# Revit family: Legrand XL³-S 160 surface mounting
name_source: partatom
category: Equipement électrique
units: mm (PartAtom-declared; Revit-internal decimal feet)

## family parameters
Basée sur le plan de construction = Non
Configuration du panneau = Deux colonnes, circuits au sein
Cote de connecteur circulaire = Utiliser le diamètre
Couper avec des vides une fois chargée = Non
Numéro OmniClass = 23.80.30.11.17
Partagée = Non
Point de calcul de pièce = Non
Titre OmniClass = Distribution Boards and Control Panels
Toujours verticalement = Oui
Type d'élément = Tableau de raccordement

## types (12) — shared parameters
ETIM Class 6.0 = EC000261
Fabricant = Legrand
General Conditions of Use = https://export.legrand.com
IK = 07
IP = 40
Image du type = XL3S160_saillie_337204_p_230125.jpg
Material = Steel
RAL = 9003
URL = www.legrand.fr
depth = 135 mm  [stored 0.442913 ft]
distance side installation zone = 135 mm  [stored 0.442913 ft]
door = Oui
zero-valued in all types: Elévation par défaut

## per-type parameters (varying)
- Distribution envelope - XL³ S 160 Métal - surface mounting - 24 modules - 2 rows: Cabinet 337202=Oui; Cabinet 337203=Non; Cabinet 337204=Non; Cabinet 337205=Non; Cabinet 337206=Non; Cabinet 337207=Non; Cabinet 337208=Non; Cabinet 337214=Non; Cabinet 337215=Non; Cabinet 337216=Non; Cabinet 337217=Non; Cabinet 337218=Non; Description=337202  Distribution envelope - XL³ S 160 Métal - surface mounting - 24 modules - 2 rows; depth installation zone=730 mm  [stored 2.39501 ft]; distance before installation zone=595 mm  [stored 1.9521 ft]; door 337252=Oui; door 337253=Non; door 337254=Non; door 337255=Non; door 337256=Non; door 337257=Non; door 337258=Non; door 337264=Non; door 337265=Non; door 337266=Non; door 337267=Non; door 337268=Non; height=440 mm  [stored 1.44357 ft]; width=595 mm  [stored 1.9521 ft]; width installation zone=865 mm  [stored 2.83793 ft]
- Distribution envelope - XL³ S 160 Métal - surface mounting - 24 modules - 3 rows: Cabinet 337202=Non; Cabinet 337203=Oui; Cabinet 337204=Non; Cabinet 337205=Non; Cabinet 337206=Non; Cabinet 337207=Non; Cabinet 337208=Non; Cabinet 337214=Non; Cabinet 337215=Non; Cabinet 337216=Non; Cabinet 337217=Non; Cabinet 337218=Non; Description=337203  Distribution envelope - XL³ S 160 Métal - surface mounting - 24 modules - 3 rows; depth installation zone=730 mm  [stored 2.39501 ft]; distance before installation zone=595 mm  [stored 1.9521 ft]; door 337252=Non; door 337253=Oui; door 337254=Non; door 337255=Non; door 337256=Non; door 337257=Non; door 337258=Non; door 337264=Non; door 337265=Non; door 337266=Non; door 337267=Non; door 337268=Non; height=590 mm  [stored 1.9357 ft]; width=595 mm  [stored 1.9521 ft]; width installation zone=865 mm  [stored 2.83793 ft]
- Distribution envelope - XL³ S 160 Métal - surface mounting - 24 modules - 4 rows: Cabinet 337202=Non; Cabinet 337203=Non; Cabinet 337204=Oui; Cabinet 337205=Non; Cabinet 337206=Non; Cabinet 337207=Non; Cabinet 337208=Non; Cabinet 337214=Non; Cabinet 337215=Non; Cabinet 337216=Non; Cabinet 337217=Non; Cabinet 337218=Non; Description=337204  Distribution envelope - XL³ S 160 Métal - surface mounting - 24 modules - 4 rows; depth installation zone=730 mm  [stored 2.39501 ft]; distance before installation zone=595 mm  [stored 1.9521 ft]; door 337252=Non; door 337253=Non; door 337254=Oui; door 337255=Non; door 337256=Non; door 337257=Non; door 337258=Non; door 337264=Non; door 337265=Non; door 337266=Non; door 337267=Non; door 337268=Non; height=740 mm  [stored 2.42782 ft]; width=595 mm  [stored 1.9521 ft]; width installation zone=865 mm  [stored 2.83793 ft]
- Distribution envelope - XL³ S 160 Métal - surface mounting - 24 modules - 5 rows: Cabinet 337202=Non; Cabinet 337203=Non; Cabinet 337204=Non; Cabinet 337205=Oui; Cabinet 337206=Non; Cabinet 337207=Non; Cabinet 337208=Non; Cabinet 337214=Non; Cabinet 337215=Non; Cabinet 337216=Non; Cabinet 337217=Non; Cabinet 337218=Non; Description=337205  Distribution envelope - XL³ S 160 Métal - surface mounting - 24 modules - 6 rows; depth installation zone=730 mm  [stored 2.39501 ft]; distance before installation zone=595 mm  [stored 1.9521 ft]; door 337252=Non; door 337253=Non; door 337254=Non; door 337255=Oui; door 337256=Non; door 337257=Non; door 337258=Non; door 337264=Non; door 337265=Non; door 337266=Non; door 337267=Non; door 337268=Non; height=890 mm  [stored 2.91995 ft]; width=595 mm  [stored 1.9521 ft]; width installation zone=865 mm  [stored 2.83793 ft]
- Distribution envelope - XL³ S 160 Métal - surface mounting - 24 modules - 6 rows: Cabinet 337202=Non; Cabinet 337203=Non; Cabinet 337204=Non; Cabinet 337205=Non; Cabinet 337206=Oui; Cabinet 337207=Non; Cabinet 337208=Non; Cabinet 337214=Non; Cabinet 337215=Non; Cabinet 337216=Non; Cabinet 337217=Non; Cabinet 337218=Non; Description=337206  Distribution envelope - XL³ S 160 Métal - surface mounting - 24 modules - 7 rows; depth installation zone=730 mm  [stored 2.39501 ft]; distance before installation zone=595 mm  [stored 1.9521 ft]; door 337252=Non; door 337253=Non; door 337254=Non; door 337255=Non; door 337256=Oui; door 337257=Non; door 337258=Non; door 337264=Non; door 337265=Non; door 337266=Non; door 337267=Non; door 337268=Non; height=1040 mm  [stored 3.41207 ft]; width=595 mm  [stored 1.9521 ft]; width installation zone=865 mm  [stored 2.83793 ft]
- Distribution envelope - XL³ S 160 Métal - surface mounting - 24 modules - 7 rows: Cabinet 337202=Non; Cabinet 337203=Non; Cabinet 337204=Non; Cabinet 337205=Non; Cabinet 337206=Non; Cabinet 337207=Oui; Cabinet 337208=Non; Cabinet 337214=Non; Cabinet 337215=Non; Cabinet 337216=Non; Cabinet 337217=Non; Cabinet 337218=Non; Description=337207  Distribution envelope - XL³ S 160 Métal - surface mounting - 24 modules - 7 rows; depth installation zone=730 mm  [stored 2.39501 ft]; distance before installation zone=595 mm  [stored 1.9521 ft]; door 337252=Non; door 337253=Non; door 337254=Non; door 337255=Non; door 337256=Non; door 337257=Oui; door 337258=Non; door 337264=Non; door 337265=Non; door 337266=Non; door 337267=Non; door 337268=Non; height=1190 mm  [stored 3.9042 ft]; width=595 mm  [stored 1.9521 ft]; width installation zone=865 mm  [stored 2.83793 ft]
- Distribution envelope - XL³ S 160 Métal - surface mounting - 24 modules - 8 rows: Cabinet 337202=Non; Cabinet 337203=Non; Cabinet 337204=Non; Cabinet 337205=Non; Cabinet 337206=Non; Cabinet 337207=Non; Cabinet 337208=Oui; Cabinet 337214=Non; Cabinet 337215=Non; Cabinet 337216=Non; Cabinet 337217=Non; Cabinet 337218=Non; Description=337208  Distribution envelope - XL³ S 160 Métal - surface mounting - 24 modules - 8 rows; depth installation zone=730 mm  [stored 2.39501 ft]; distance before installation zone=595 mm  [stored 1.9521 ft]; door 337252=Non; door 337253=Non; door 337254=Non; door 337255=Non; door 337256=Non; door 337257=Non; door 337258=Oui; door 337264=Non; door 337265=Non; door 337266=Non; door 337267=Non; door 337268=Non; height=1340 mm  [stored 4.39633 ft]; width=595 mm  [stored 1.9521 ft]; width installation zone=865 mm  [stored 2.83793 ft]
- Distribution envelope - XL³ S 160 Métal - surface mounting - 36 modules - 4 rows: Cabinet 337202=Non; Cabinet 337203=Non; Cabinet 337204=Non; Cabinet 337205=Non; Cabinet 337206=Non; Cabinet 337207=Non; Cabinet 337208=Non; Cabinet 337214=Oui; Cabinet 337215=Non; Cabinet 337216=Non; Cabinet 337217=Non; Cabinet 337218=Non; Description=337214  Distribution envelope - XL³ S 160 Métal - surface mounting - 36 modules - 4 rows; depth installation zone=945 mm; distance before installation zone=810 mm; door 337252=Non; door 337253=Non; door 337254=Non; door 337255=Non; door 337256=Non; door 337257=Non; door 337258=Non; door 337264=Oui; door 337265=Non; door 337266=Non; door 337267=Non; door 337268=Non; height=740 mm  [stored 2.42782 ft]; width=810 mm; width installation zone=1080 mm  [stored 3.54331 ft]
- Distribution envelope - XL³ S 160 Métal - surface mounting - 36 modules - 5 rows: Cabinet 337202=Non; Cabinet 337203=Non; Cabinet 337204=Non; Cabinet 337205=Non; Cabinet 337206=Non; Cabinet 337207=Non; Cabinet 337208=Non; Cabinet 337214=Non; Cabinet 337215=Oui; Cabinet 337216=Non; Cabinet 337217=Non; Cabinet 337218=Non; Description=337215  Distribution envelope - XL³ S 160 Métal - surface mounting - 36 modules - 5 rows; depth installation zone=945 mm; distance before installation zone=810 mm; door 337252=Non; door 337253=Non; door 337254=Non; door 337255=Non; door 337256=Non; door 337257=Non; door 337258=Non; door 337264=Non; door 337265=Oui; door 337266=Non; door 337267=Non; door 337268=Non; height=890 mm  [stored 2.91995 ft]; width=810 mm; width installation zone=1080 mm  [stored 3.54331 ft]
- Distribution envelope - XL³ S 160 Métal - surface mounting - 36 modules - 6 rows: Cabinet 337202=Non; Cabinet 337203=Non; Cabinet 337204=Non; Cabinet 337205=Non; Cabinet 337206=Non; Cabinet 337207=Non; Cabinet 337208=Non; Cabinet 337214=Non; Cabinet 337215=Non; Cabinet 337216=Oui; Cabinet 337217=Non; Cabinet 337218=Non; Description=337216  Distribution envelope - XL³ S 160 Métal - surface mounting - 36 modules - 6 rows; depth installation zone=945 mm; distance before installation zone=810 mm; door 337252=Non; door 337253=Non; door 337254=Non; door 337255=Non; door 337256=Non; door 337257=Non; door 337258=Non; door 337264=Non; door 337265=Non; door 337266=Oui; door 337267=Non; door 337268=Non; height=1040 mm  [stored 3.41207 ft]; width=810 mm; width installation zone=1080 mm  [stored 3.54331 ft]
- Distribution envelope - XL³ S 160 Métal - surface mounting - 36 modules - 7 rows: Cabinet 337202=Non; Cabinet 337203=Non; Cabinet 337204=Non; Cabinet 337205=Non; Cabinet 337206=Non; Cabinet 337207=Non; Cabinet 337208=Non; Cabinet 337214=Non; Cabinet 337215=Non; Cabinet 337216=Non; Cabinet 337217=Oui; Cabinet 337218=Non; Description=337217  Distribution envelope - XL³ S 160 Métal - surface mounting - 36 modules - 7 rows; depth installation zone=945 mm; distance before installation zone=810 mm; door 337252=Non; door 337253=Non; door 337254=Non; door 337255=Non; door 337256=Non; door 337257=Non; door 337258=Non; door 337264=Non; door 337265=Non; door 337266=Non; door 337267=Oui; door 337268=Non; height=1190 mm  [stored 3.9042 ft]; width=810 mm; width installation zone=1080 mm  [stored 3.54331 ft]
- Distribution envelope - XL³ S 160 Métal - surface mounting - 36 modules - 8 rows: Cabinet 337202=Non; Cabinet 337203=Non; Cabinet 337204=Non; Cabinet 337205=Non; Cabinet 337206=Non; Cabinet 337207=Non; Cabinet 337208=Non; Cabinet 337214=Non; Cabinet 337215=Non; Cabinet 337216=Non; Cabinet 337217=Non; Cabinet 337218=Oui; Description=337218  Distribution envelope - XL³ S 160 Métal - surface mounting - 36 modules - 8 rows; depth installation zone=945 mm; distance before installation zone=810 mm; door 337252=Non; door 337253=Non; door 337254=Non; door 337255=Non; door 337256=Non; door 337257=Non; door 337258=Non; door 337264=Non; door 337265=Non; door 337266=Non; door 337267=Non; door 337268=Oui; height=1340 mm  [stored 4.39633 ft]; width=810 mm; width installation zone=1080 mm  [stored 3.54331 ft]

note: [stored X ft] marks values corroborated as IEEE doubles in the binary element streams (Revit-internal decimal feet)
